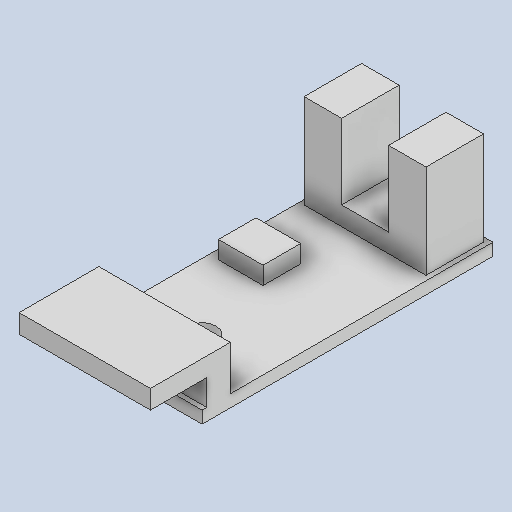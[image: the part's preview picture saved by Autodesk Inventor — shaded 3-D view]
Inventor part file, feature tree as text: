
AUTODESK INVENTOR PART (.ipt)
format: ipt  version: 2022 (Build 260153070, 153G)  size: 159,232 bytes
history: native  units: in
note: dims shown in document units (in); Inventor stores cm internally (conversion verified against a paired STEP export)
features: extrude x5, sketch x3
ambient origin geometry x8: Origin, YZ Plane, XZ Plane, XY Plane, X Axis, Y Axis, Z Axis, Center Point
bodies: Solid1 (feature_tree)
feature tree (8):
  sketch  "Sketch1"  dims[d0=0.5512in d1=1.2205in]
  extrude  "Extrusion1"  Depth=1.2205in
  extrude  "Extrusion2"  Depth=0.5118in
  extrude  "Extrusion3"  Depth=0.0197in
  extrude  "Extrusion4"  Depth=0.1181in
  extrude  "Extrusion5"  Depth=0.315in
  sketch  "Sketch2"  dims[d2=0.0197in d3=0.5118in]
  sketch  "Sketch3"  dims[d4=0.2411in d5=0.0197in d7=0.1181in d8=0.2756in d9=0.0394in d10=0.5807in d11=0.1575in d12=0.187in d13=0.0512in d14=0.0in d15=0.0787in d16=0.0in d17=0.0738in d18=0.0in d19=0.1575in d20=0.1575in d21=0.315in d22=0.0in d23=0.187in d24=0.0984in d25=0.0197in d26=0.3346in d27=0.0787in d28=0.315in d29=0.0in]
